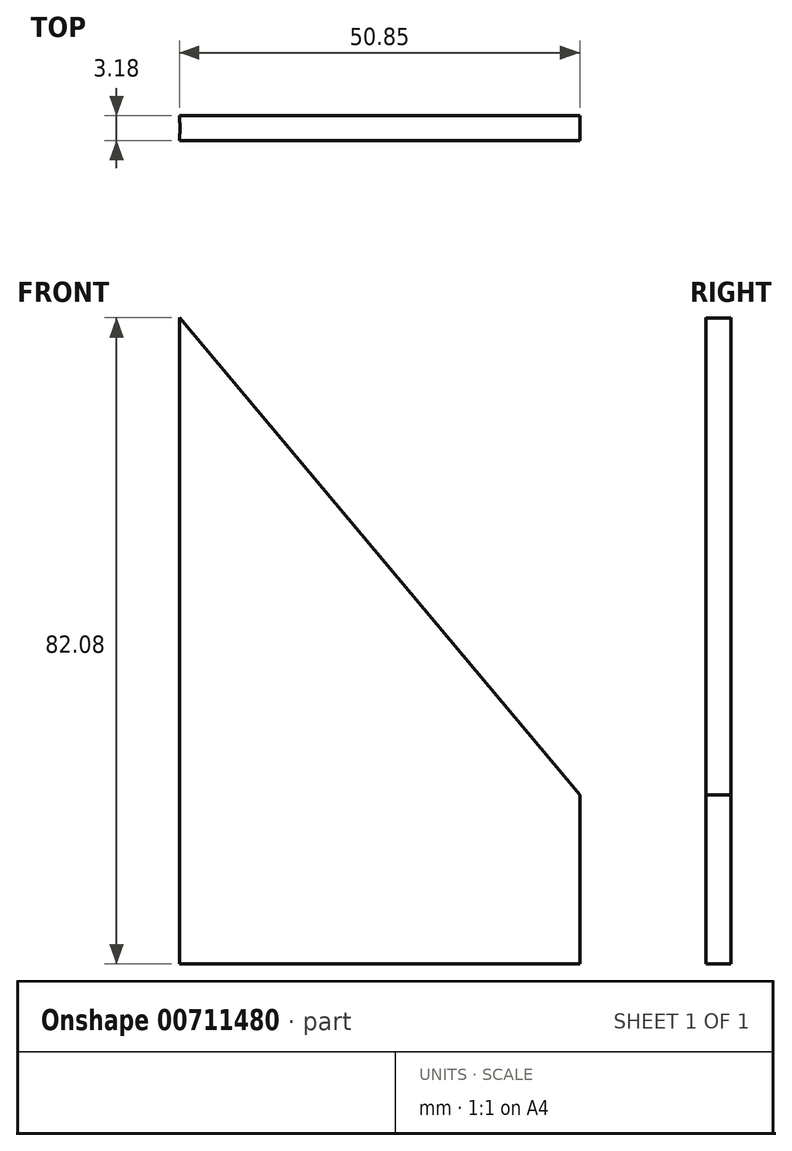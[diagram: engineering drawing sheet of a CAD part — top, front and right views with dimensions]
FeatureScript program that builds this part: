
annotation { "Feature Type Name" : "Feature", "Feature Type Description" : "" }
export const myFeature = defineFeature(function(context is Context, id is Id, definition is map)
    precondition{}
    {
        {
            var Q0;
            Q0=qCreatedBy(makeId("Top.planeOp"),FACE);
            var sketch = newSketch(context, id + "F0", { "sketchPlane" : qUnion([Q0])});
            skLineSegment(sketch, "E0", {"start": v(0, 0) * mm, "end": v(-26.99, 0) * mm, "construction": true});
            skArc(sketch, "E1", {"start": v(-0.05, -1.59) * mm, "mid": v(0, 0) * mm, "end": v(-0.05, 1.59) * mm});
            skLineSegment(sketch, "E2", {"start": v(0, -1.59) * mm, "end": v(-0.05, -1.59) * mm});
            skLineSegment(sketch, "E3", {"start": v(0, 0) * mm, "end": v(50.8, 0) * mm, "construction": true});
            skLineSegment(sketch, "E4", {"start": v(0, 0) * mm, "end": v(0, 1.59) * mm, "construction": true});
            skLineSegment(sketch, "E5", {"start": v(0, 1.59) * mm, "end": v(-0.05, 1.59) * mm});
            skLineSegment(sketch, "E6", {"start": v(0, 1.59) * mm, "end": v(50.8, 1.59) * mm});
            skLineSegment(sketch, "E7", {"start": v(50.8, 0) * mm, "end": v(50.8, 1.59) * mm});
            skLineSegment(sketch, "E8", {"start": v(50.8, 0) * mm, "end": v(50.8, -1.59) * mm});
            skLineSegment(sketch, "E9", {"start": v(50.8, -1.59) * mm, "end": v(0, -1.59) * mm});
            skSolve(sketch);
        }
        {
            var Q0;
            Q0=makeQuery(id+"F0.imprint","IMPRINT",FACE,{"disambiguationData":[TD([[makeQuery(id+"F0.imprint","IMPRINT",EDGE,{"derivedFrom":sQuery(id+"F0.wireOp",EDGE,"E1")}),-1.0]])]});
            extrude(context, id + "F1", {"entities" : qUnion([Q0]), "depth" : 88.9 * mm, "offsetDistance" : 25.4 * mm});
        }
        {
            var Q0;
            Q0=qCreatedBy(makeId("Front.planeOp"),FACE);
            var sketch = newSketch(context, id + "F2", { "sketchPlane" : qUnion([Q0])});
            skLineSegment(sketch, "E10", {"start": v(0, 0) * mm, "end": v(63.5, 0) * mm, "construction": true});
            skLineSegment(sketch, "E11", {"start": v(63.5, 0) * mm, "end": v(63.5, 6.35) * mm, "construction": true});
            skLineSegment(sketch, "E12", {"start": v(63.5, 6.35) * mm, "end": v(-15.3, 100.26) * mm});
            skLineSegment(sketch, "E13", {"start": v(-15.3, 100.26) * mm, "end": v(63.5, 100.26) * mm});
            skLineSegment(sketch, "E14", {"start": v(63.5, 100.26) * mm, "end": v(63.5, 6.35) * mm});
            skSolve(sketch);
        }
        {
            var Q0;
            Q0 = qSketchRegion(id + "F2", true);
            extrude(context, id + "F3", {"entities" : qUnion([Q0]), "operationType" : NewBodyOperationType.REMOVE, "endBound" : BoundingType.SYMMETRIC, "oppositeDirection" : true, "depth" : 25.4 * mm, "offsetDistance" : 25.4 * mm});
        }
    });
